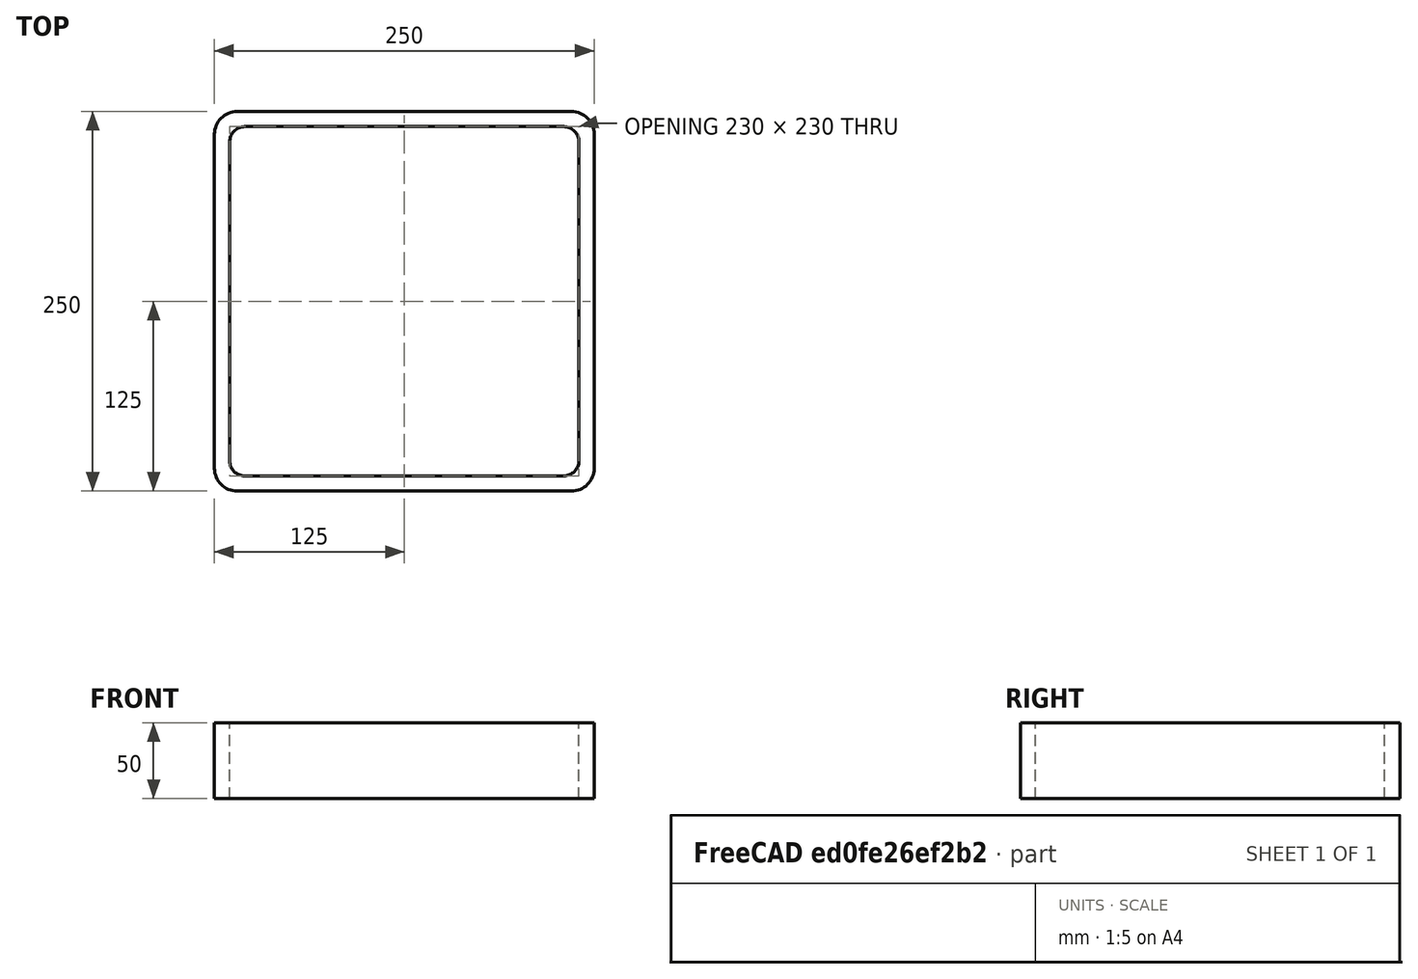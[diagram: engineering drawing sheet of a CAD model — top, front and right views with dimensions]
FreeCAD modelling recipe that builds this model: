
FCSTD DOCUMENT  (FreeCAD 0.15R4671 (Git))
Label: Square hollow section 250x250x10 EN10219 S235JRH
License: All rights reserved
LicenseURL: http://en.wikipedia.org/wiki/All_rights_reserved
objects: Sketcher::SketchObject×1, Part::Extrusion×1
note: 2 computed .brp shape members not serialized (recipe doc carries the construction recipe); baked Part::Feature solids carry a one-line shape summary decoded from their .brp

FEATURE [Sketcher::SketchObject] Sketch
  sketch-geometry (16):
    g0: LineSegment StartX=-105 StartY=115 StartZ=0 EndX=105 EndY=115 EndZ=0
    g1: LineSegment StartX=115 StartY=105 StartZ=0 EndX=115 EndY=-105 EndZ=0
    g2: LineSegment StartX=105 StartY=-115 StartZ=0 EndX=-105 EndY=-115 EndZ=0
    g3: LineSegment StartX=-115 StartY=-105 StartZ=0 EndX=-115 EndY=105 EndZ=0
    g4: LineSegment StartX=-110 StartY=125 StartZ=0 EndX=110 EndY=125 EndZ=0
    g5: LineSegment StartX=125 StartY=110 StartZ=0 EndX=125 EndY=-110 EndZ=0
    g6: LineSegment StartX=110 StartY=-125 StartZ=0 EndX=-110 EndY=-125 EndZ=0
    g7: LineSegment StartX=-125 StartY=-110 StartZ=0 EndX=-125 EndY=110 EndZ=0
    g8: ArcOfCircle CenterX=-105 CenterY=105 CenterZ=0 NormalX=0 NormalY=0 NormalZ=1 Radius=10 StartAngle=1.5708 EndAngle=3.14159
    g9: ArcOfCircle CenterX=105 CenterY=105 CenterZ=0 NormalX=0 NormalY=0 NormalZ=1 Radius=10 StartAngle=0 EndAngle=1.5708
    g10: ArcOfCircle CenterX=105 CenterY=-105 CenterZ=0 NormalX=0 NormalY=0 NormalZ=1 Radius=10 StartAngle=4.71239 EndAngle=6.28319
    g11: ArcOfCircle CenterX=-105 CenterY=-105 CenterZ=0 NormalX=0 NormalY=0 NormalZ=1 Radius=10 StartAngle=3.14159 EndAngle=4.71239
    g12: ArcOfCircle CenterX=110 CenterY=110 CenterZ=0 NormalX=0 NormalY=0 NormalZ=1 Radius=15 StartAngle=0 EndAngle=1.5708
    g13: ArcOfCircle CenterX=110 CenterY=-110 CenterZ=0 NormalX=0 NormalY=0 NormalZ=1 Radius=15 StartAngle=4.71239 EndAngle=6.28319
    g14: ArcOfCircle CenterX=-110 CenterY=-110 CenterZ=0 NormalX=0 NormalY=0 NormalZ=1 Radius=15 StartAngle=3.14159 EndAngle=4.71239
    g15: ArcOfCircle CenterX=-110 CenterY=110 CenterZ=0 NormalX=0 NormalY=0 NormalZ=1 Radius=15 StartAngle=1.5708 EndAngle=3.14159
  constraints (36):
    c: Horizontal(g2)
    c: Vertical(g3)
    c: Horizontal(g6)
    c: Vertical(g7)
    c: Tangent(g3,g8) = 1.5708
    c: Tangent(g0,g8) = 1.5708
    c: Tangent(g0,g9) = 1.5708
    c: Tangent(g1,g9) = 1.5708
    c: Tangent(g1,g10) = 1.5708
    c: Tangent(g2,g10) = 1.5708
    c: Tangent(g2,g11) = 1.5708
    c: Tangent(g3,g11) = 1.5708
    c: Tangent(g4,g12) = 1.5708
    c: Tangent(g5,g12) = 1.5708
    c: Tangent(g5,g13) = 1.5708
    c: Tangent(g6,g13) = 1.5708
    c: Tangent(g6,g14) = 1.5708
    c: Tangent(g7,g14) = 1.5708
    c: Tangent(g7,g15) = 1.5708
    c: Tangent(g4,g15) = 1.5708
    c: Equal(g9,g8)
    c: Equal(g9,g11)
    c: Equal(g9,g10)
    c: Equal(g12,g15)
    c: Equal(g12,g14)
    c: Equal(g12,g13)
    c: Symmetric(g4,g6,g-1)
    c: Symmetric(g7,g5,g-2)
    c: DistanceY(g4,g6) = -250
    c: DistanceX(g7,g5) = 250
    c: Symmetric(g3,g1,g-2)
    c: Symmetric(g0,g2,g-1)
    c: DistanceY(g0,g4) = 10
    c: DistanceX(g5,g1) = -10
    c: Radius(g9) = 10
    c: Radius(g12) = 15
FEATURE [Part::Extrusion] Extrude  label="Square hollow section 250x250x10 EN10219 S235JRH"
  Base = -> Sketch
  Dir = (0,0,50)
  Solid = true
